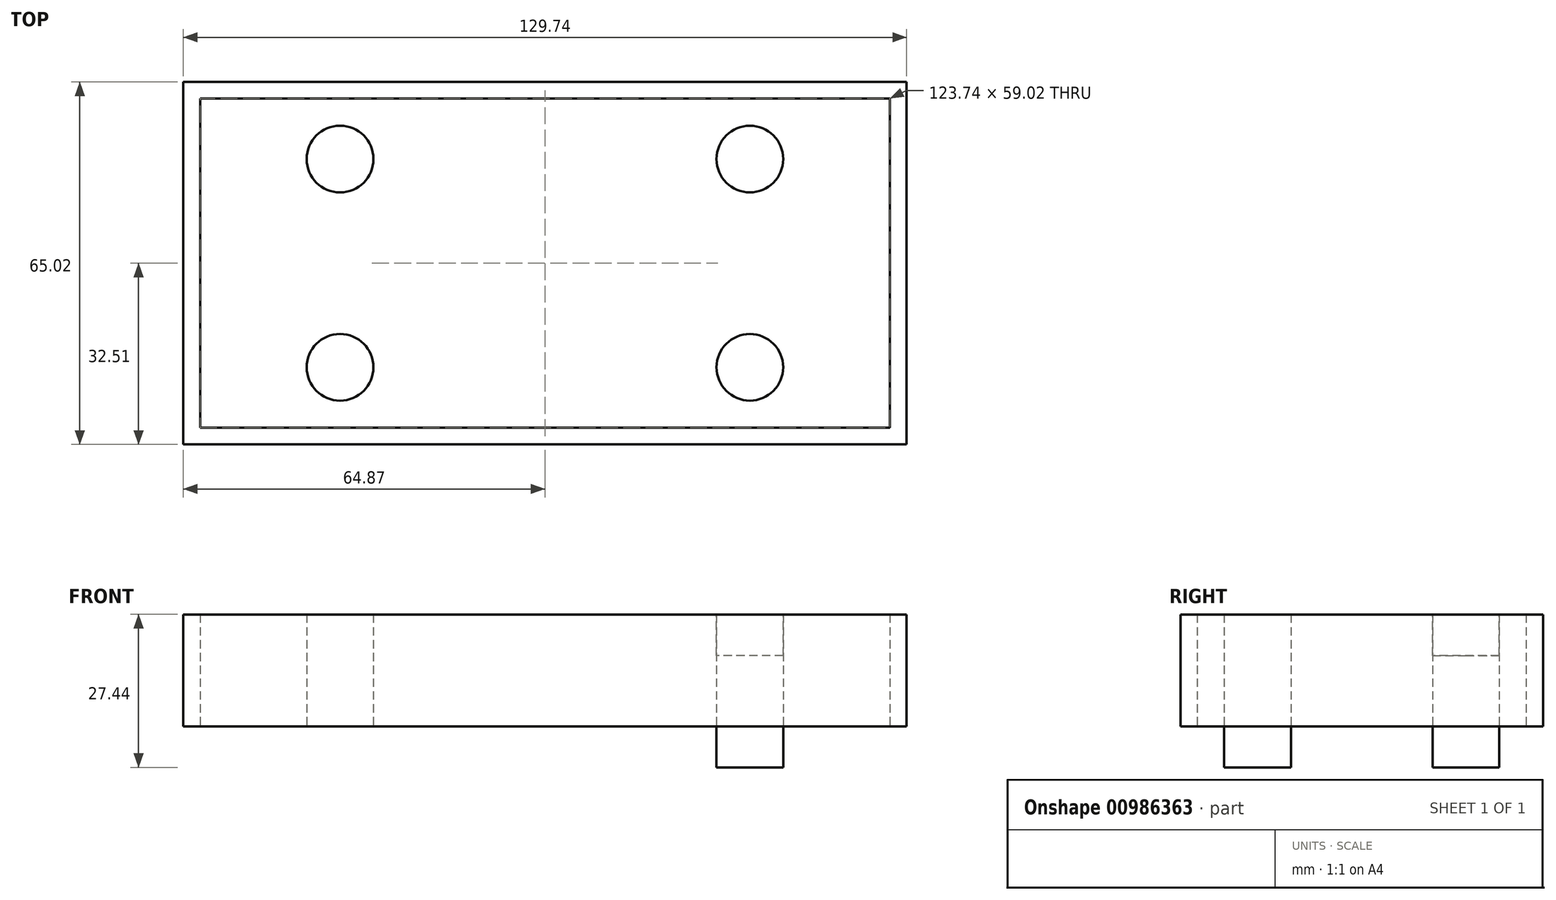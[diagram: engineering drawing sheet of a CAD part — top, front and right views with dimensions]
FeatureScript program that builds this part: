
annotation { "Feature Type Name" : "Feature", "Feature Type Description" : "" }
export const myFeature = defineFeature(function(context is Context, id is Id, definition is map)
    precondition{}
    {
        {
            var Q0;
            Q0=qCreatedBy(makeId("Top.planeOp"),FACE);
            var sketch = newSketch(context, id + "F0", { "sketchPlane" : qUnion([Q0])});
            skLineSegment(sketch, "E0.bottom", {"start": v(61.87, 29.5) * mm, "end": v(-61.87, 29.5) * mm});
            skLineSegment(sketch, "E0.top", {"start": v(61.87, -29.5) * mm, "end": v(-61.87, -29.5) * mm});
            skLineSegment(sketch, "E0.left", {"start": v(61.87, 29.5) * mm, "end": v(61.87, -29.5) * mm});
            skLineSegment(sketch, "E0.right", {"start": v(-61.87, 29.5) * mm, "end": v(-61.87, -29.5) * mm});
            skPoint(sketch, "E0.middle", {"position": v(0, 0) * mm});
            skLineSegment(sketch, "E1.0", {"start": v(64.87, 32.5) * mm, "end": v(-64.87, 32.5) * mm});
            skLineSegment(sketch, "E1.1", {"start": v(64.87, 32.5) * mm, "end": v(64.87, -32.5) * mm});
            skLineSegment(sketch, "E1.2", {"start": v(64.87, -32.5) * mm, "end": v(-64.87, -32.5) * mm});
            skLineSegment(sketch, "E1.3", {"start": v(-64.87, 32.5) * mm, "end": v(-64.87, -32.5) * mm});
            skLineSegment(sketch, "E2.bottom", {"start": v(36.75, -18.68) * mm, "end": v(-36.75, -18.68) * mm, "construction": true});
            skLineSegment(sketch, "E2.top", {"start": v(36.75, 18.68) * mm, "end": v(-36.75, 18.68) * mm, "construction": true});
            skLineSegment(sketch, "E2.left", {"start": v(36.75, -18.68) * mm, "end": v(36.75, 18.68) * mm, "construction": true});
            skLineSegment(sketch, "E2.right", {"start": v(-36.75, -18.68) * mm, "end": v(-36.75, 18.68) * mm, "construction": true});
            skCircle(sketch, "E3", {"center": v(-36.75, 18.68) * mm, "radius": 5.98 * mm});
            skCircle(sketch, "E4", {"center": v(36.75, 18.68) * mm, "radius": 5.98 * mm});
            skCircle(sketch, "E5", {"center": v(36.75, -18.68) * mm, "radius": 5.98 * mm});
            skCircle(sketch, "E6", {"center": v(-36.75, -18.68) * mm, "radius": 5.98 * mm});
            skSolve(sketch);
        }
        {
            var Q0;
            Q0=makeQuery(id+"F0.imprint","IMPRINT",FACE,{"disambiguationData":[TD([[makeQuery(id+"F0.imprint","IMPRINT",EDGE,{"derivedFrom":sQuery(id+"F0.wireOp",EDGE,"E5")}),1.0]])]});
            var Q1;
            Q1=makeQuery(id+"F0.imprint","IMPRINT",FACE,{"disambiguationData":[TD([[makeQuery(id+"F0.imprint","IMPRINT",EDGE,{"derivedFrom":sQuery(id+"F0.wireOp",EDGE,"E6")}),1.0]])]});
            var Q2;
            Q2=makeQuery(id+"F0.imprint","IMPRINT",FACE,{"disambiguationData":[TD([[makeQuery(id+"F0.imprint","IMPRINT",EDGE,{"derivedFrom":sQuery(id+"F0.wireOp",EDGE,"E4")}),1.0]])]});
            var Q3;
            Q3=makeQuery(id+"F0.imprint","IMPRINT",FACE,{"disambiguationData":[TD([[makeQuery(id+"F0.imprint","IMPRINT",EDGE,{"derivedFrom":sQuery(id+"F0.wireOp",EDGE,"E0.bottom")}),-1.0]])]});
            var Q4;
            Q4=makeQuery(id+"F0.imprint","IMPRINT",FACE,{"disambiguationData":[TD([[makeQuery(id+"F0.imprint","IMPRINT",EDGE,{"derivedFrom":sQuery(id+"F0.wireOp",EDGE,"E3")}),1.0]])]});
            extrude(context, id + "F1", {"entities" : qUnion([Q0, Q1, Q2, Q3, Q4]), "depth" : 20.07 * mm, "offsetDistance" : 25.4 * mm});
        }
        {
            var Q0;
            Q0=makeQuery(id+"F1.opExtrude","CAP_FACE",FACE,{"disambiguationData":[OSD([sQuery(id+"F0.wireOp",EDGE,"E5")])],"isStart":true});
            var Q1;
            Q1=makeQuery(id+"F1.opExtrude","CAP_FACE",FACE,{"disambiguationData":[OSD([sQuery(id+"F0.wireOp",EDGE,"E4")])],"isStart":false});
            var Q2;
            Q2=makeQuery(id+"F1.opExtrude","CAP_FACE",FACE,{"disambiguationData":[OSD([sQuery(id+"F0.wireOp",EDGE,"E4")])],"isStart":true});
            extrude(context, id + "F2", {"entities" : qUnion([Q0, Q1, Q2]), "depth" : 7.37 * mm, "offsetDistance" : 25.4 * mm});
        }
    });
